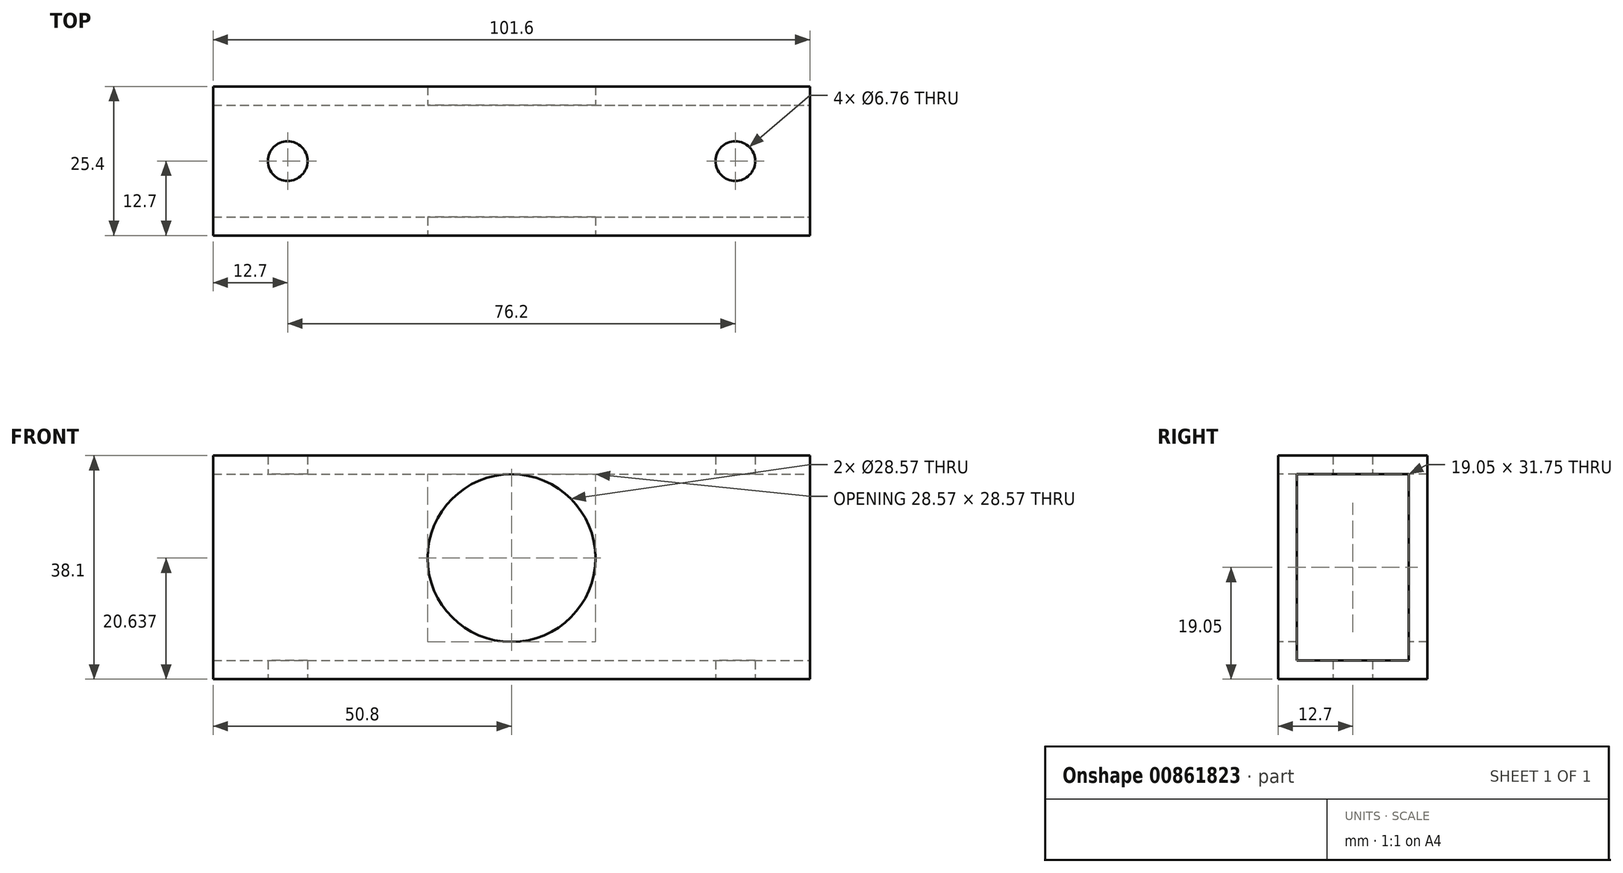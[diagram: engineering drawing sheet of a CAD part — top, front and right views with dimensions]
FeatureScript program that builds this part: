
annotation { "Feature Type Name" : "Feature", "Feature Type Description" : "" }
export const myFeature = defineFeature(function(context is Context, id is Id, definition is map)
    precondition{}
    {
        {
            var Q0;
            Q0=qCreatedBy(makeId("Top.planeOp"),FACE);
            var sketch = newSketch(context, id + "F0", { "sketchPlane" : qUnion([Q0])});
            skLineSegment(sketch, "E0.bottom", {"start": v(-50.8, 12.7) * mm, "end": v(50.8, 12.7) * mm});
            skLineSegment(sketch, "E0.top", {"start": v(-50.8, -12.7) * mm, "end": v(50.8, -12.7) * mm});
            skLineSegment(sketch, "E0.left", {"start": v(-50.8, 12.7) * mm, "end": v(-50.8, -12.7) * mm});
            skLineSegment(sketch, "E0.right", {"start": v(50.8, 12.7) * mm, "end": v(50.8, -12.7) * mm});
            skCircle(sketch, "E1", {"center": v(-38.1, 0) * mm, "radius": 3.38 * mm});
            skCircle(sketch, "E2", {"center": v(38.1, 0) * mm, "radius": 3.38 * mm});
            skLineSegment(sketch, "E3", {"start": v(-50.8, 12.7) * mm, "end": v(50.8, -12.7) * mm, "construction": true});
            skSolve(sketch);
        }
        {
            var Q0;
            Q0=makeQuery(id+"F0.imprint","IMPRINT",FACE,{"disambiguationData":[TD([[makeQuery(id+"F0.imprint","IMPRINT",EDGE,{"derivedFrom":sQuery(id+"F0.wireOp",EDGE,"E0.bottom")}),-1.0]])]});
            extrude(context, id + "F1", {"entities" : qUnion([Q0]), "depth" : 38.1 * mm, "offsetDistance" : 25.4 * mm});
        }
        {
            var Q0;
            Q0=makeQuery(id+"F1.opExtrude","SWEPT_FACE",FACE,{"disambiguationData":[OSD([sQuery(id+"F0.wireOp",EDGE,"E0.top")])]});
            var sketch = newSketch(context, id + "F2", { "sketchPlane" : qUnion([Q0])});
            skCircle(sketch, "E4", {"center": v(0, 20.64) * mm, "radius": 14.29 * mm});
            skLineSegment(sketch, "E5", {"start": v(0, 38.1) * mm, "end": v(0, 0) * mm, "construction": true});
            skSolve(sketch);
        }
        {
            var Q0;
            {var subQ0=sQuery(id+"F2.wireOp",EDGE,"umpgv6YI-j2qE-5yQA-K5WO-RXtPKTKVNCdC");Q0=makeQuery(id+"F2.imprint","IMPRINT",FACE,{"disambiguationData":[TD([[makeQuery(id+"F2.imprint","IMPRINT",EDGE,{"derivedFrom":subQ0}),1.0]])]});}
            var Q1;
            {var subQ0=sQuery(id+"F2.wireOp",EDGE,"Y1e5f35R-TGia-lU1D-7UJm-yEdCw5gScNMN");Q1=makeQuery(id+"F2.imprint","IMPRINT",FACE,{"disambiguationData":[TD([[makeQuery(id+"F2.imprint","IMPRINT",EDGE,{"derivedFrom":subQ0}),-1.0]])]});}
            var Q2;
            Q2=makeQuery(id+"F2.imprint","IMPRINT",FACE,{"disambiguationData":[TD([[makeQuery(id+"F2.imprint","IMPRINT",EDGE,{"derivedFrom":sQuery(id+"F2.wireOp",EDGE,"E4")}),1.0]])]});
            extrude(context, id + "F3", {"entities" : qUnion([Q0, Q1, Q2]), "operationType" : NewBodyOperationType.REMOVE, "oppositeDirection" : true, "depth" : 25.4 * mm, "offsetDistance" : 25.4 * mm});
        }
        {
            var Q0;
            Q0=qCreatedBy(makeId("Right.planeOp"),FACE);
            var sketch = newSketch(context, id + "F4", { "sketchPlane" : qUnion([Q0])});
            skLineSegment(sketch, "E6.bottom", {"start": v(9.52, 34.93) * mm, "end": v(-9.53, 34.93) * mm});
            skLineSegment(sketch, "E6.top", {"start": v(9.53, 3.18) * mm, "end": v(-9.52, 3.18) * mm});
            skLineSegment(sketch, "E6.left", {"start": v(9.52, 34.93) * mm, "end": v(9.53, 3.18) * mm});
            skLineSegment(sketch, "E6.right", {"start": v(-9.53, 34.93) * mm, "end": v(-9.52, 3.18) * mm});
            skSolve(sketch);
        }
        {
            var Q0;
            Q0 = qSketchRegion(id + "F4", true);
            extrude(context, id + "F5", {"entities" : qUnion([Q0]), "operationType" : NewBodyOperationType.REMOVE, "endBound" : BoundingType.THROUGH_ALL, "oppositeDirection" : true, "depth" : 25.4 * mm, "offsetDistance" : 25.4 * mm, "hasSecondDirection" : true, "secondDirectionBound" : BoundingType.THROUGH_ALL, "secondDirectionOppositeDirection" : false, "secondDirectionDepth" : 25.4 * mm});
        }
    });
